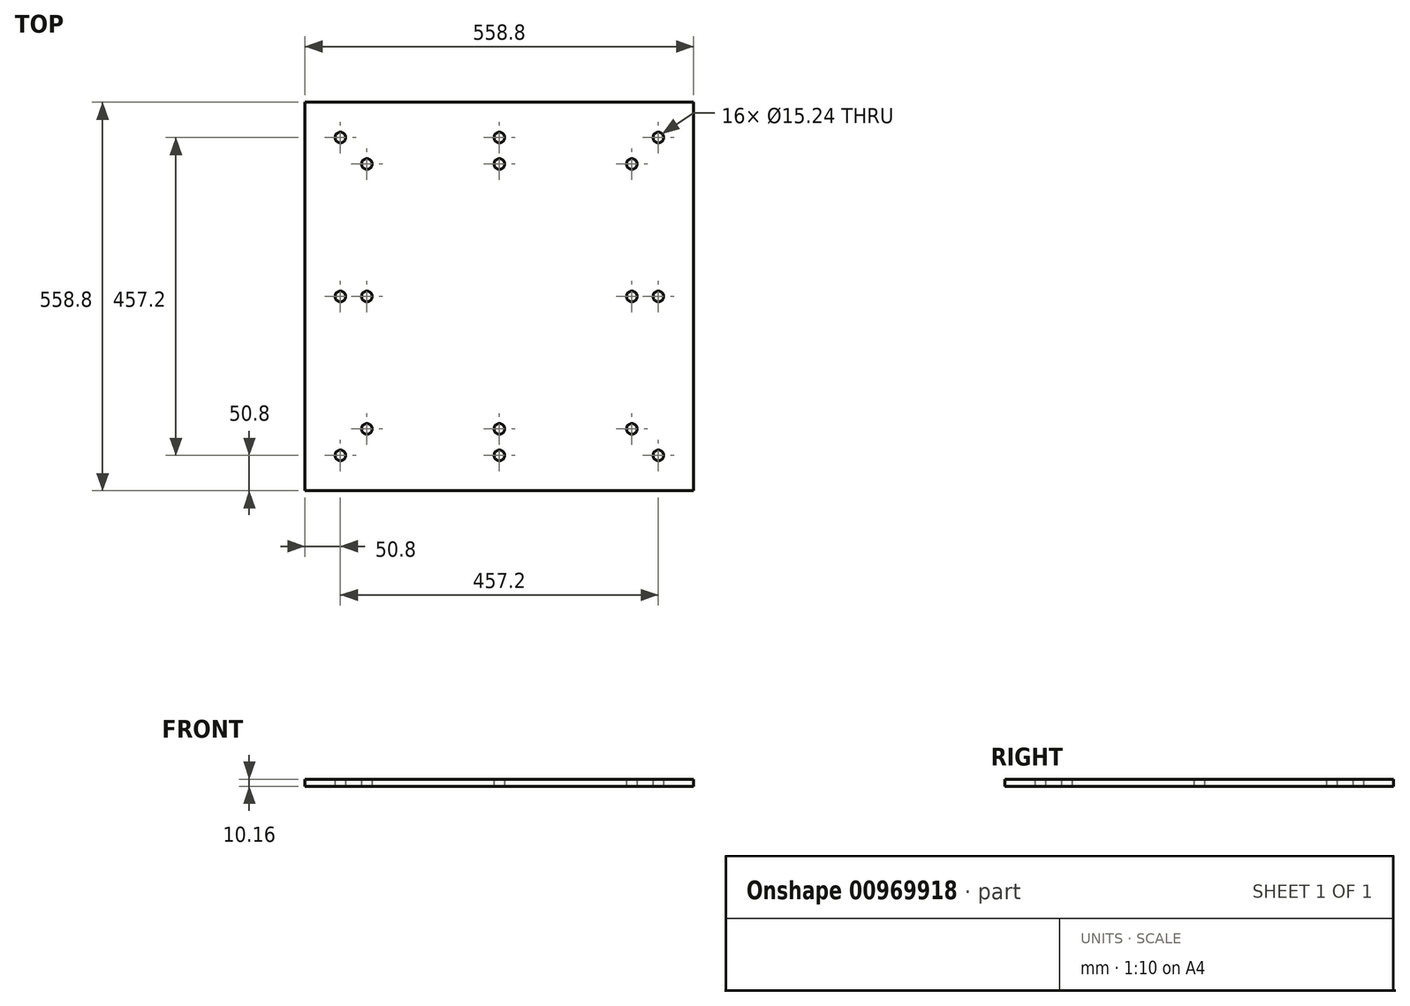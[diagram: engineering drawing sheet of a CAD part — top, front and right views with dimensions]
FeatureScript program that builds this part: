
annotation { "Feature Type Name" : "Feature", "Feature Type Description" : "" }
export const myFeature = defineFeature(function(context is Context, id is Id, definition is map)
    precondition{}
    {
        {
            var Q0;
            Q0=qCreatedBy(makeId("Top.planeOp"),FACE);
            var sketch = newSketch(context, id + "F0", { "sketchPlane" : qUnion([Q0])});
            skLineSegment(sketch, "E0.bottom", {"start": v(279.4, 279.4) * mm, "end": v(-279.4, 279.4) * mm});
            skLineSegment(sketch, "E0.top", {"start": v(279.4, -279.4) * mm, "end": v(-279.4, -279.4) * mm});
            skLineSegment(sketch, "E0.left", {"start": v(279.4, 279.4) * mm, "end": v(279.4, -279.4) * mm});
            skLineSegment(sketch, "E0.right", {"start": v(-279.4, 279.4) * mm, "end": v(-279.4, -279.4) * mm});
            skPoint(sketch, "E0.middle", {"position": v(0, 0) * mm});
            skCircle(sketch, "E1", {"center": v(-190.5, 190.5) * mm, "radius": 7.62 * mm});
            skCircle(sketch, "E2", {"center": v(0, 190.5) * mm, "radius": 7.62 * mm});
            skCircle(sketch, "E3", {"center": v(190.5, 190.5) * mm, "radius": 7.62 * mm});
            skCircle(sketch, "E4", {"center": v(228.6, 228.6) * mm, "radius": 7.62 * mm});
            skCircle(sketch, "E5", {"center": v(0, 228.6) * mm, "radius": 7.62 * mm});
            skCircle(sketch, "E6", {"center": v(-228.6, 228.6) * mm, "radius": 7.62 * mm});
            skCircle(sketch, "E7", {"center": v(-228.6, -228.6) * mm, "radius": 7.62 * mm});
            skCircle(sketch, "E8", {"center": v(0, -228.6) * mm, "radius": 7.62 * mm});
            skCircle(sketch, "E9", {"center": v(228.6, -228.6) * mm, "radius": 7.62 * mm});
            skCircle(sketch, "E10", {"center": v(190.5, -190.5) * mm, "radius": 7.62 * mm});
            skCircle(sketch, "E11", {"center": v(0, -190.5) * mm, "radius": 7.62 * mm});
            skCircle(sketch, "E12", {"center": v(-190.5, -190.5) * mm, "radius": 7.62 * mm});
            skCircle(sketch, "E13", {"center": v(-190.5, 0) * mm, "radius": 7.62 * mm});
            skCircle(sketch, "E14", {"center": v(-228.6, 0) * mm, "radius": 7.62 * mm});
            skCircle(sketch, "E15", {"center": v(190.5, 0) * mm, "radius": 7.62 * mm});
            skCircle(sketch, "E16", {"center": v(228.6, 0) * mm, "radius": 7.62 * mm});
            skSolve(sketch);
        }
        {
            var Q0;
            Q0=makeQuery(id+"F0.imprint","IMPRINT",FACE,{"disambiguationData":[TD([[makeQuery(id+"F0.imprint","IMPRINT",EDGE,{"derivedFrom":sQuery(id+"F0.wireOp",EDGE,"E0.bottom")}),1.0]])]});
            extrude(context, id + "F1", {"entities" : qUnion([Q0]), "depth" : 10.16 * mm, "offsetDistance" : 25.4 * mm});
        }
    });
